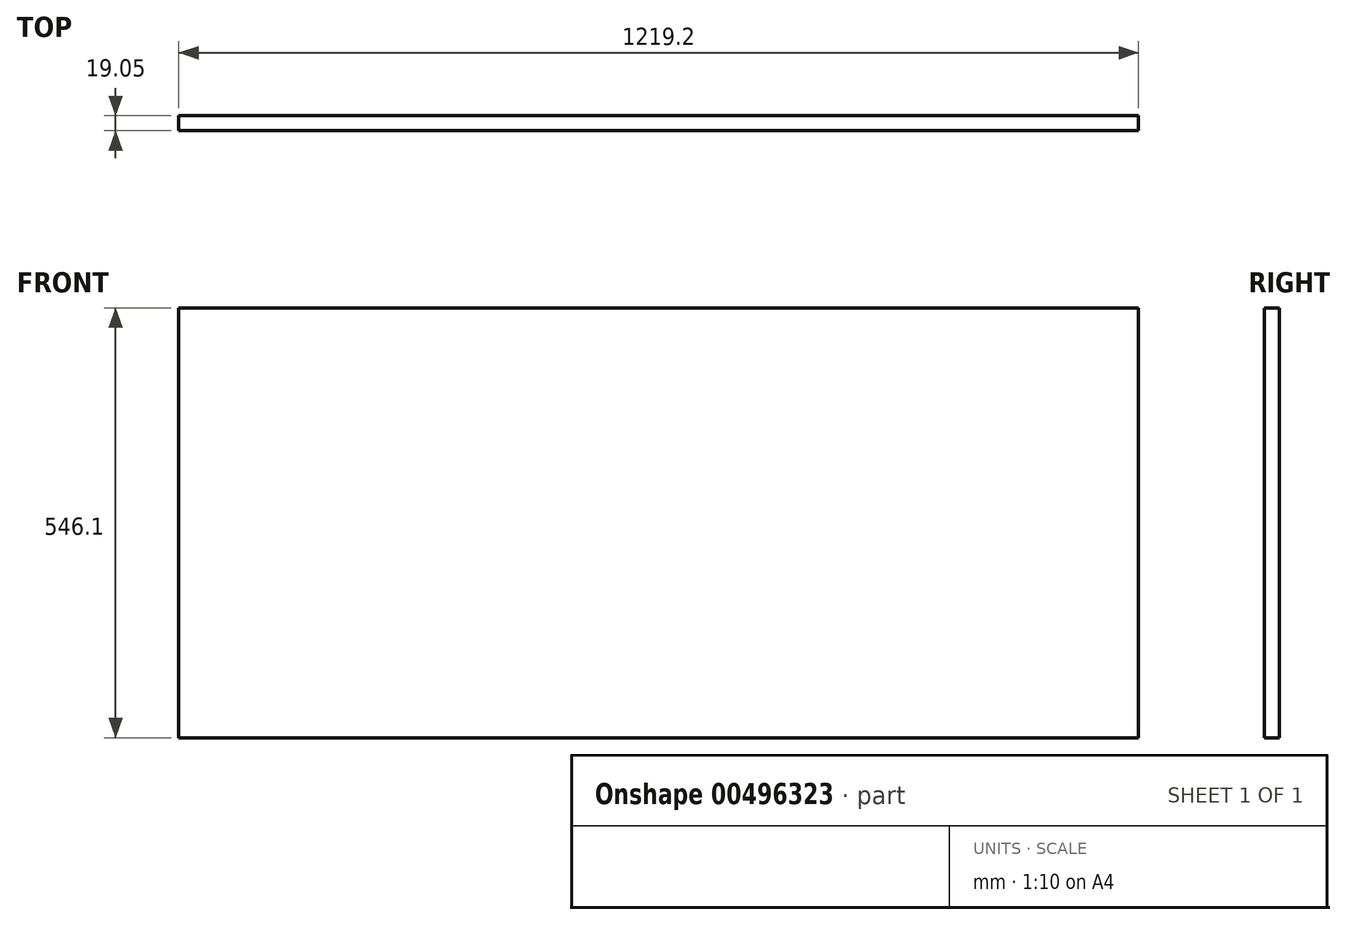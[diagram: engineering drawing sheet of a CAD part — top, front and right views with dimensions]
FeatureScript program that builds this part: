
annotation { "Feature Type Name" : "Feature", "Feature Type Description" : "" }
export const myFeature = defineFeature(function(context is Context, id is Id, definition is map)
    precondition{}
    {
        {
            var Q0;
            Q0=qCreatedBy(makeId("Front.planeOp"),FACE);
            var sketch = newSketch(context, id + "F0", { "sketchPlane" : qUnion([Q0])});
            skLineSegment(sketch, "E0.bottom", {"start": v(609.6, -273.05) * mm, "end": v(-609.6, -273.05) * mm});
            skLineSegment(sketch, "E0.top", {"start": v(609.6, 273.05) * mm, "end": v(-609.6, 273.05) * mm});
            skLineSegment(sketch, "E0.left", {"start": v(609.6, -273.05) * mm, "end": v(609.6, 273.05) * mm});
            skLineSegment(sketch, "E0.right", {"start": v(-609.6, -273.05) * mm, "end": v(-609.6, 273.05) * mm});
            skPoint(sketch, "E0.middle", {"position": v(0, 0) * mm});
            skSolve(sketch);
        }
        {
            var Q0;
            Q0 = qSketchRegion(id + "F0", true);
            extrude(context, id + "F1", {"entities" : qUnion([Q0]), "depth" : 19.05 * mm, "offsetDistance" : 25.4 * mm});
        }
    });
